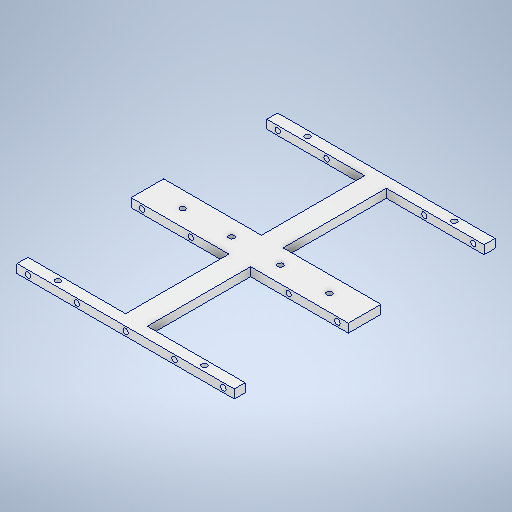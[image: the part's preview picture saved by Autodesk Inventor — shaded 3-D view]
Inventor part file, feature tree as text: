
AUTODESK INVENTOR PART (.ipt)
format: ipt  version: 2025.1 (Build 291241000, 241)  size: 338,944 bytes
history: native  units: mm
features: sketch x4, hole x3, extrude x1, plane x1, mirror x1
ambient origin geometry x8: Origin, YZ Plane, XZ Plane, XY Plane, X Axis, Y Axis, Z Axis, Center Point
bodies: Solid1 (feature_tree)
feature tree (10):
  extrude  "Extrusion1"  Depth=200.0mm
  hole  "Hole1"  [1 undecoded]
  hole  "Hole2"  [1 undecoded]
  plane  "Work Plane1"
  mirror  "Mirror1"
  hole  "Hole3"  [1 undecoded]
  sketch  "Sketch1"  dims[d0=10.0mm d1=200.0mm]
  sketch  "Sketch2"  dims[d2=20.0mm d3=30.0mm]
  sketch  "Sketch3"  dims[d4=10.0mm d5=95.0mm]
  sketch  "Sketch4"  dims[d6=95.0mm d7=8.0mm d8=0.0mm d9=15.0mm d10=67.5mm d11=45.0mm d12=45.0mm d13=45.0mm d14=67.5mm d15=135.0mm d16=5.0mm d17=6.0mm d18=4.0mm d19=2.0mm d20=90.0deg d21=8.0mm d22=0.0mm d23=4.0mm d24=45.0mm d25=90.0mm d26=90.0mm d27=45.0mm d28=5.0mm d29=6.0mm d30=4.0mm d31=2.0mm d32=90.0deg d33=8.0mm d34=0.0mm d35=120.0mm d36=4.0mm d37=180.0mm d38=90.0mm d39=45.0mm d41=5.0mm d42=6.0mm d43=4.0mm d44=2.0mm d45=90.0deg d46=8.0mm d47=0.0mm d48=45.0mm]
note: 3 required parameter values undecoded (feature->parameter linkage not recoverable at this tier; creation-order binding heuristic only, values carry confidence <= 0.55)
